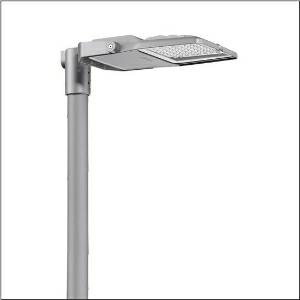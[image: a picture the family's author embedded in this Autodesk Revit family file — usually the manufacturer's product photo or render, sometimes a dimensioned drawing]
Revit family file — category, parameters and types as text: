
# Revit family: floodlight_fl_21_iq_mini___pl61_5xa7772d2c3a_9c70
name_source: partatom
category: Lighting Fixtures
units: mm (PartAtom-declared; Revit-internal decimal feet)

## family parameters
Cut with Voids When Loaded = No
Host = Face
Light Source = No
Part Type = Normal
Room Calculation Point = No
Round Connector Dimension = Use Diameter
Shared = No

## types (1)
- --- (1 x LED, 17500 lm, 143 W, 3000K)
    Apparent Load = 143 VA
    CIE Flux Codes = 33 65 98 100 100
    Color Rendering = 70
    Color Temperature = 3000K
    Default Elevation = 1800 mm
    Description = Floodlight FL 21 iQ mini, floodlight, primary light control with lens, of PMMA, primary optical cover: protective disc, of toughened safety glass, transparent, light distribution: PL61, light emission: direct distribution, installation type: surface-mounted, LED, High Power LED, rated luminous flux: 17.500lm, luminous efficacy: 122lm/W, light colour: 730, colour temperature: 3000K, control gear: iQ Street-Remote/DALI, control: Auto-Match, Temp-Guard, Night-Set, Smart-Wire, Desk-Remote (wireless, voltage-free reading and setting of iQ features in the workshop via application-optimized NFC function/RFID function), optimised constant luminous flux control (CLO 2.0), Light-Fading, Lumen-Switch, with terminal, 6-pole, mains connection: 220..240V, AC, 50/60Hz, start of lifetime: 143W, end of service life: 152W, reduction: 61W, luminaire housing, of diecast aluminium, powder-coated, Siteco® metallic grey (DB 702S), corrosivity category C5 mid according to DIN EN ISO 12944, suitable for swimming pools, chlorine-resistant, sealing non-destructively replaceable, please order mast flange separately, mast bracket, of steel, galvanised, powder-coated, protection rating (complete): IP66, insulation class (complete): insulation class II (safety insulation), certification: CE, ENEC, VDE, protection symbol: D, impact resistance: IK08, permissible operating ambient temperature: -40..+40°C, permissible operating ambient temperature for outdoor applications: -40..+50°C, standard: DIN EN 12944, LABS conformity tested according to VDMA 24364:2018-05, packaging unit: 1 piece

Light Distribution: PL61
    Height = 70 mm
    Lamp = 1 x LED
    Lamp Light Flux = 17500 lm
    Lamp Power = 143 W
    Lamp count = 1
    Length = 485 mm
    Luminous efficacy = 122 lm/W
    Manufacturer = Siteco
    ModVariant = No
    Model = 5XA7772D2C3A
    Number of Poles = 1
    OnlyDefault = Yes
    Power Factor = 1
    Product Name = Floodlight FL 21 iQ mini | PL61
    Product group = floodlight | pylon annexe
    ProductGroupID = 6201
    Protection Class = Protection class II
    Protection Degree = IP 66
    RLX_Detail_Level = 1
    RLX_Emergency_Light_Flux = 0 lm
    RLX_Emergency_Type = 0
    RLX_Emergency_Type_DB = No
    RlxData = <blob elided: 101709 chars, md5=decd34e7>
    Socket = socket
    Standby Power = 0 W
    System Light Flux = 17500 lm
    System Power = 143 W
    Type Comments = factory setting: luminous flux: 100 % | dim-lin: 254 | 730 mA
    Type Image = l_1007125.jpg
    URL = http://relux.com
    VarID = @adj_193925
    Voltage = 0 V
    Weight = 0.00 kg
    Width = 337 mm

## geometry (parser evidence)
native form markers: Blend x4, Sweep x11
no freeform markers — native parametric forms only
